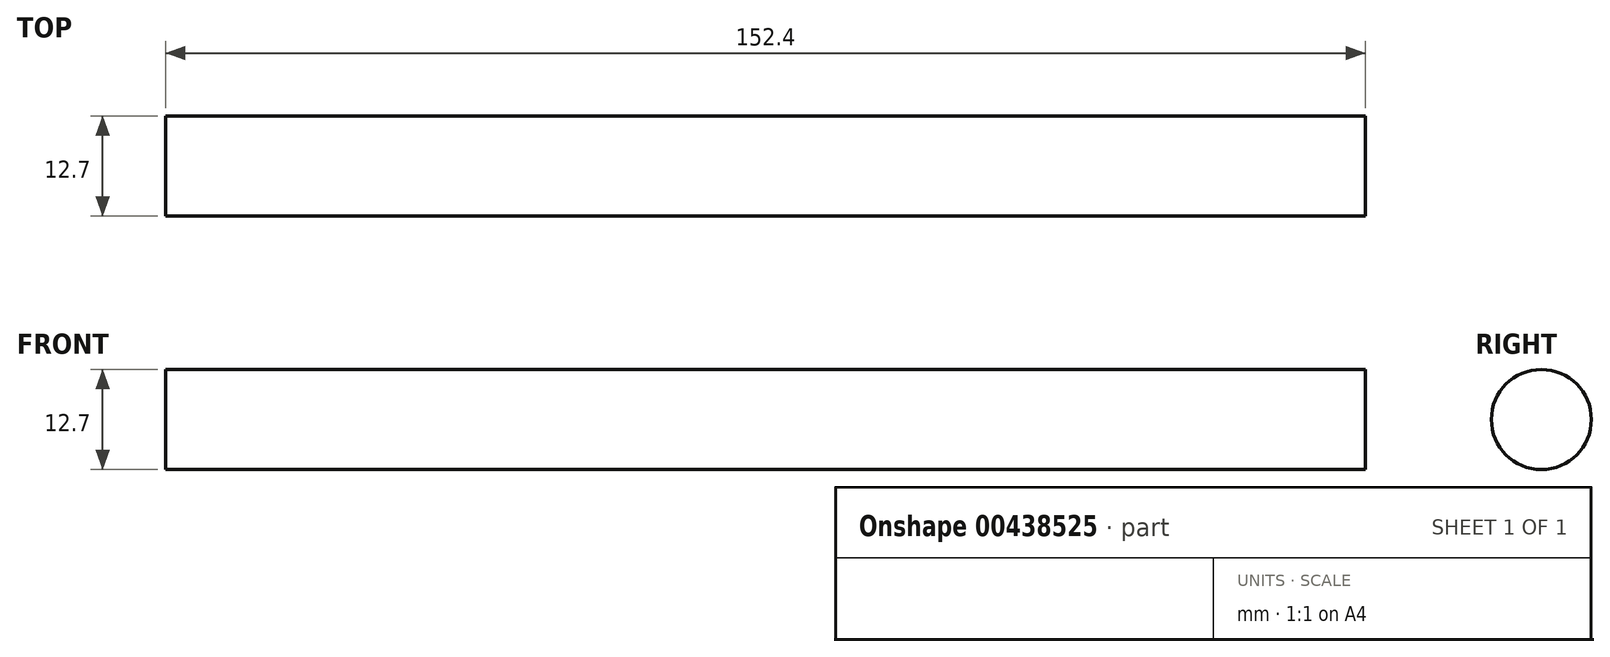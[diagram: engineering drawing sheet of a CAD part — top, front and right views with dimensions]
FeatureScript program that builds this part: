
annotation { "Feature Type Name" : "Feature", "Feature Type Description" : "" }
export const myFeature = defineFeature(function(context is Context, id is Id, definition is map)
    precondition{}
    {
        {
            var Q0;
            Q0=qCreatedBy(makeId("Right.planeOp"),FACE);
            var sketch = newSketch(context, id + "F0", { "sketchPlane" : qUnion([Q0])});
            skCircle(sketch, "E0", {"center": v(0, 0) * mm, "radius": 6.35 * mm});
            skSolve(sketch);
        }
        {
            var Q0;
            Q0=makeQuery(id+"F0.imprint","IMPRINT",FACE,{"disambiguationData":[TD([[makeQuery(id+"F0.imprint","IMPRINT",EDGE,{"derivedFrom":sQuery(id+"F0.wireOp",EDGE,"E0")}),1.0]])]});
            extrude(context, id + "F1", {"entities" : qUnion([Q0]), "depth" : 152.4 * mm});
        }
    });
